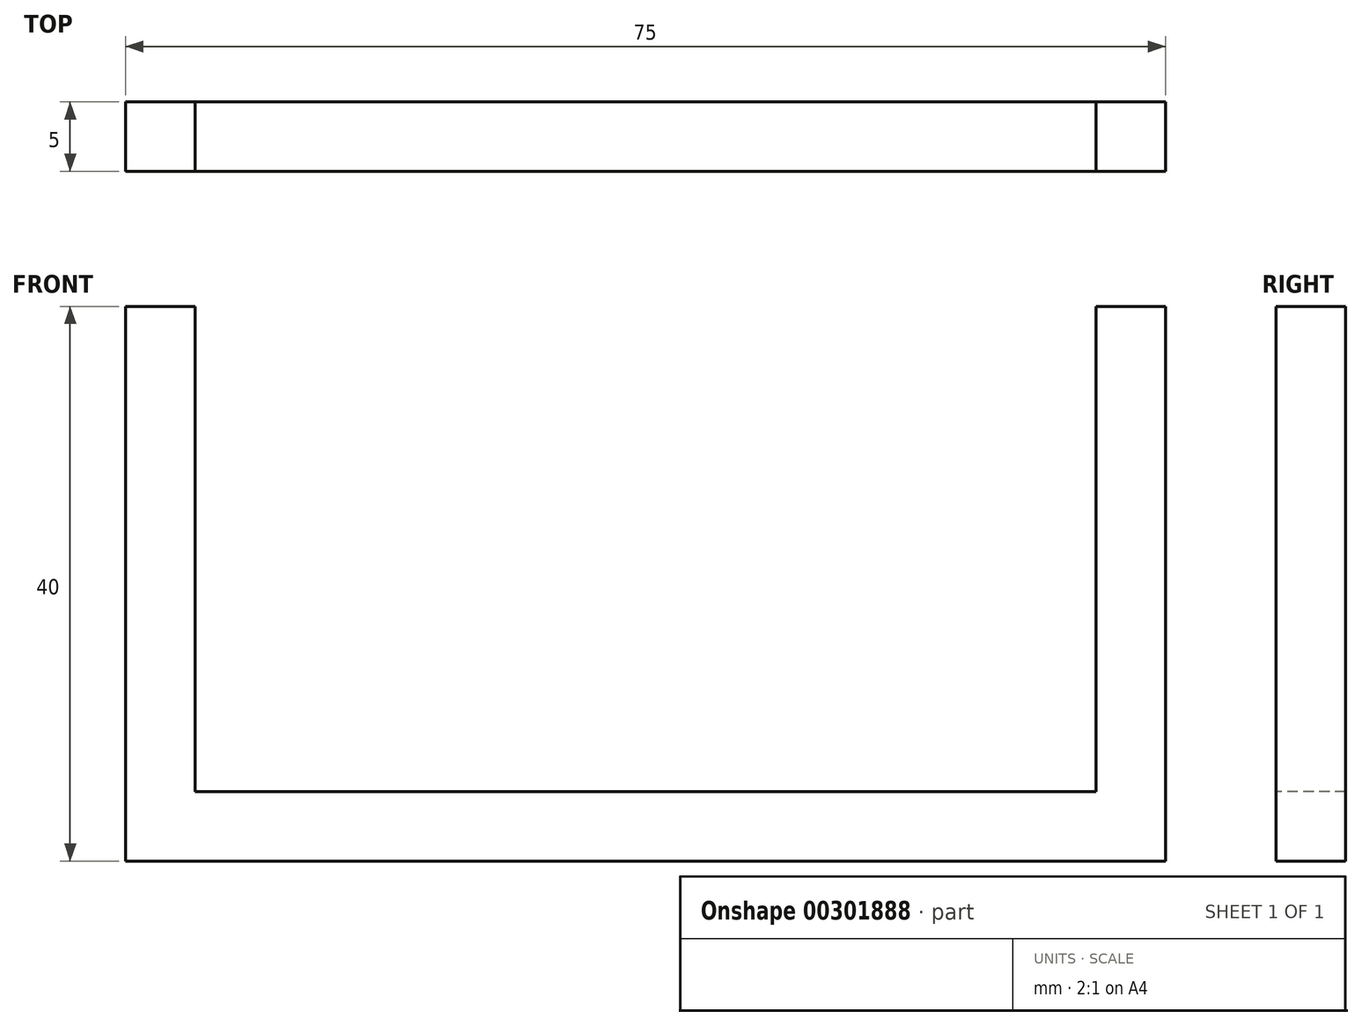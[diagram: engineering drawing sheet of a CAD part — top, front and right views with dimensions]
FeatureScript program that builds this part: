
annotation { "Feature Type Name" : "Feature", "Feature Type Description" : "" }
export const myFeature = defineFeature(function(context is Context, id is Id, definition is map)
    precondition{}
    {
        {
            var Q0;
            Q0=qCreatedBy(makeId("Front.planeOp"),FACE);
            var sketch = newSketch(context, id + "F0", { "sketchPlane" : qUnion([Q0])});
            skLineSegment(sketch, "E0.bottom", {"start": v(0, 0) * mm, "end": v(-75, 0) * mm});
            skLineSegment(sketch, "E0.top", {"start": v(0, 40) * mm, "end": v(-75, 40) * mm});
            skLineSegment(sketch, "E0.left", {"start": v(0, 0) * mm, "end": v(0, 40) * mm});
            skLineSegment(sketch, "E0.right", {"start": v(-75, 0) * mm, "end": v(-75, 40) * mm});
            skLineSegment(sketch, "E1", {"start": v(-70, 40) * mm, "end": v(-70, 5) * mm});
            skLineSegment(sketch, "E2", {"start": v(-70, 5) * mm, "end": v(-5, 5) * mm});
            skLineSegment(sketch, "E3", {"start": v(-5, 5) * mm, "end": v(-5, 40) * mm});
            skSolve(sketch);
        }
        {
            var Q0;
            Q0=makeQuery(id+"F0.imprint","IMPRINT",FACE,{"disambiguationData":[TD([[makeQuery(id+"F0.imprint","IMPRINT",EDGE,{"derivedFrom":sQuery(id+"F0.wireOp",EDGE,"E0.bottom")}),-1.0]])]});
            extrude(context, id + "F1", {"entities" : qUnion([Q0]), "oppositeDirection" : true, "depth" : 5 * mm, "offsetDistance" : 25 * mm});
        }
    });
